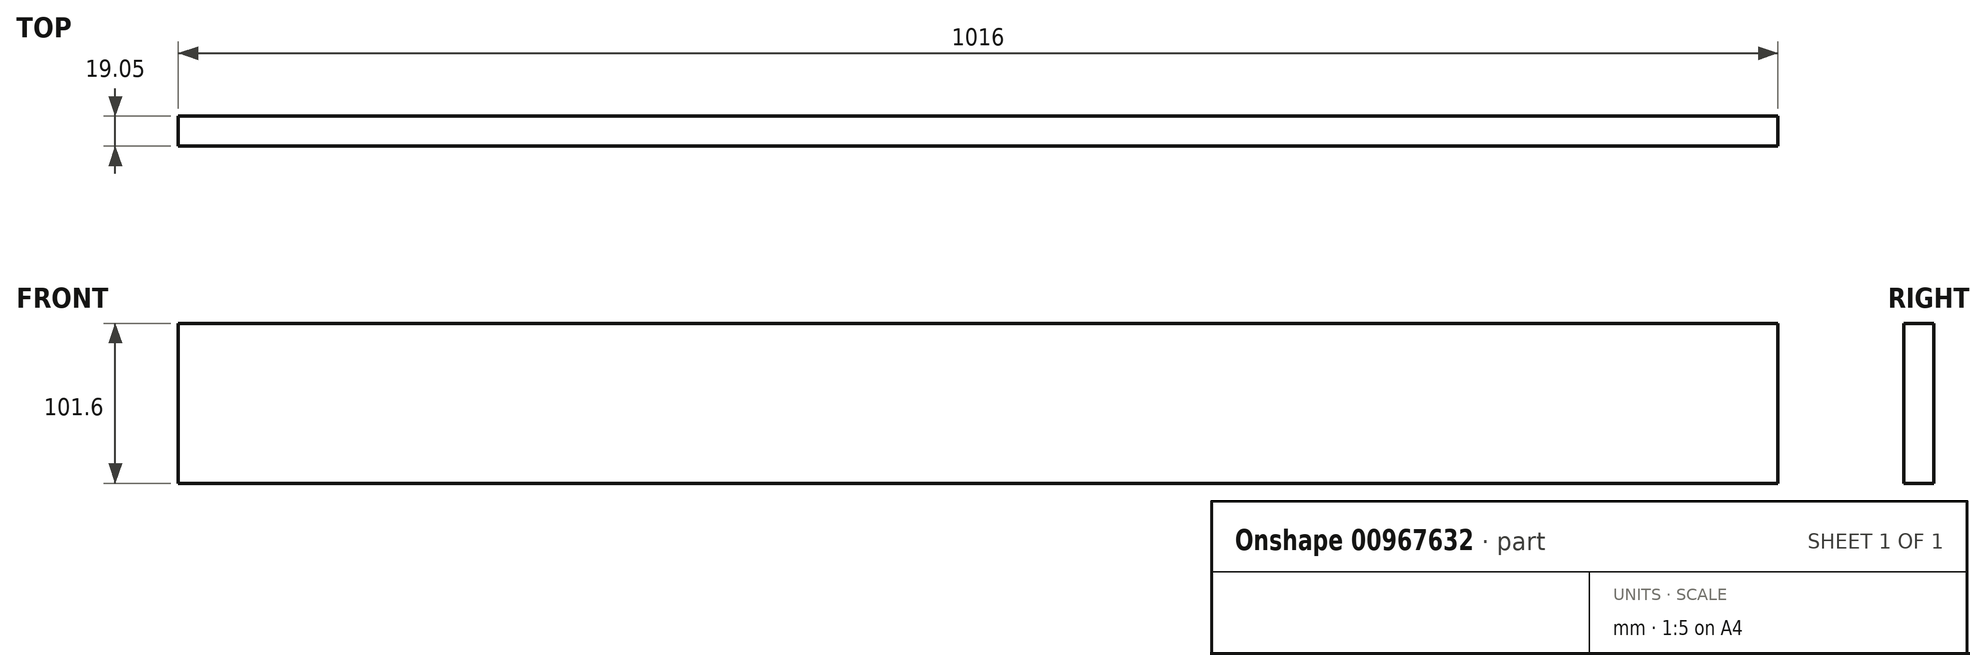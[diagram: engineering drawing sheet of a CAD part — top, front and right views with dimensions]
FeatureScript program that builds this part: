
annotation { "Feature Type Name" : "Feature", "Feature Type Description" : "" }
export const myFeature = defineFeature(function(context is Context, id is Id, definition is map)
    precondition{}
    {
        {
            var Q0;
            Q0=qCreatedBy(makeId("Front.planeOp"),FACE);
            var sketch = newSketch(context, id + "F0", { "sketchPlane" : qUnion([Q0])});
            skLineSegment(sketch, "E0.bottom", {"start": v(508, 50.8) * mm, "end": v(-508, 50.8) * mm});
            skLineSegment(sketch, "E0.top", {"start": v(508, -50.8) * mm, "end": v(-508, -50.8) * mm});
            skLineSegment(sketch, "E0.left", {"start": v(508, 50.8) * mm, "end": v(508, -50.8) * mm});
            skLineSegment(sketch, "E0.right", {"start": v(-508, 50.8) * mm, "end": v(-508, -50.8) * mm});
            skPoint(sketch, "E0.middle", {"position": v(0, 0) * mm});
            skSolve(sketch);
        }
        {
            var Q0;
            Q0 = qSketchRegion(id + "F0", true);
            extrude(context, id + "F1", {"entities" : qUnion([Q0]), "depth" : 19.05 * mm, "offsetDistance" : 25.4 * mm});
        }
    });
